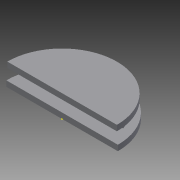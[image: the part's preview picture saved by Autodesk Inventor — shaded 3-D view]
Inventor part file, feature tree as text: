
AUTODESK INVENTOR PART (.ipt)
format: ipt  version: 2015 (Build 190159000, 159)  size: 118,784 bytes
history: native  units: mm
features: sketch x8, extrude x7
ambient origin geometry x8: Origin, YZ Plane, XZ Plane, XY Plane, X Axis, Y Axis, Z Axis, Center Point
bodies: Solid1 (feature_tree)
feature tree (15):
  extrude  "Extrusion1"  Depth=1.0mm TaperAngle=0.0deg
  extrude  "Extrusion2"  Depth=2.0mm TaperAngle=0.0deg
  extrude  "Extrusion3"  Depth=1.0mm
  extrude  "Extrusion4"  Depth=6.5mm
  sketch  "Sketch5"  dims[d11=1.75mm d12=3.25mm]
  extrude  "Extrusion5"  Depth=3.25mm
  extrude  "Extrusion6"  Depth=7.0mm TaperAngle=0.0deg
  extrude  "Extrusion7"  Depth=3.0mm TaperAngle=0.0deg
  sketch  "Sketch1"  dims[d0=20.0mm d1=1.0mm d2=0.0mm]
  sketch  "Sketch2"  dims[d3=17.0mm d4=2.0mm d5=0.0mm]
  sketch  "Sketch3"  dims[d6=1.0mm d7=0.0mm d8=9.0mm]
  sketch  "Sketch4"  dims[d9=3.5mm d10=6.5mm]
  sketch  "Sketch6"  dims[d13=7.0mm d14=0.0mm d15=7.0mm d16=0.0mm]
  sketch  "Sketch7"  dims[d17=10.0mm d18=0.0mm d19=3.0mm d20=0.0mm]
  sketch  "Sketch8"
